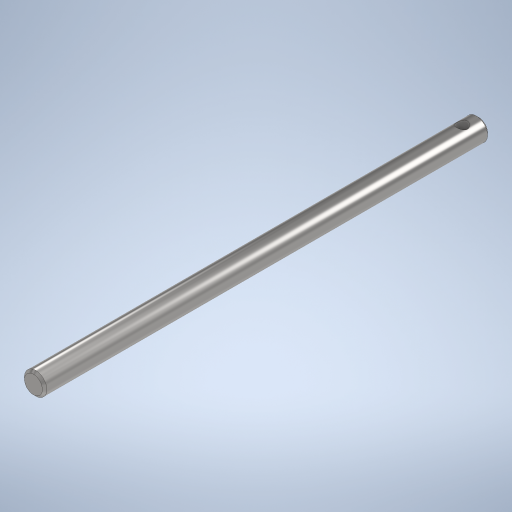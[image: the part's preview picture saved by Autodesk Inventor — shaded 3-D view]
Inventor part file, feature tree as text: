
AUTODESK INVENTOR PART (.ipt)
format: ipt  version: 2023 (Build 270158030, 158C)  size: 283,136 bytes
history: mixed  units: in
note: dims shown in document units (in); Inventor stores cm internally (conversion verified against a paired STEP export)
features: extrude x1, sketch x1, chamfer x1, imported_body x1
ambient origin geometry x8: Origin, YZ Plane, XZ Plane, XY Plane, X Axis, Y Axis, Z Axis, Center Point
bodies: Solid1 (imported_parasolid)
feature tree (4):
  extrude  "Extrusion2"  Depth=0.1969in
  sketch  "Sketch3"  dims[d3=0.1969in d4=0.2953in d5=0.0in d6=0.0in]
  chamfer  "Chamfer1"  [1 undecoded]
  imported_body  NMx_Import_Brep_tag  [imported B-rep: ~5 faces, bbox_mm=None]
note: 1 required parameter value undecoded (feature->parameter linkage not recoverable at this tier; creation-order binding heuristic only, values carry confidence <= 0.55)
